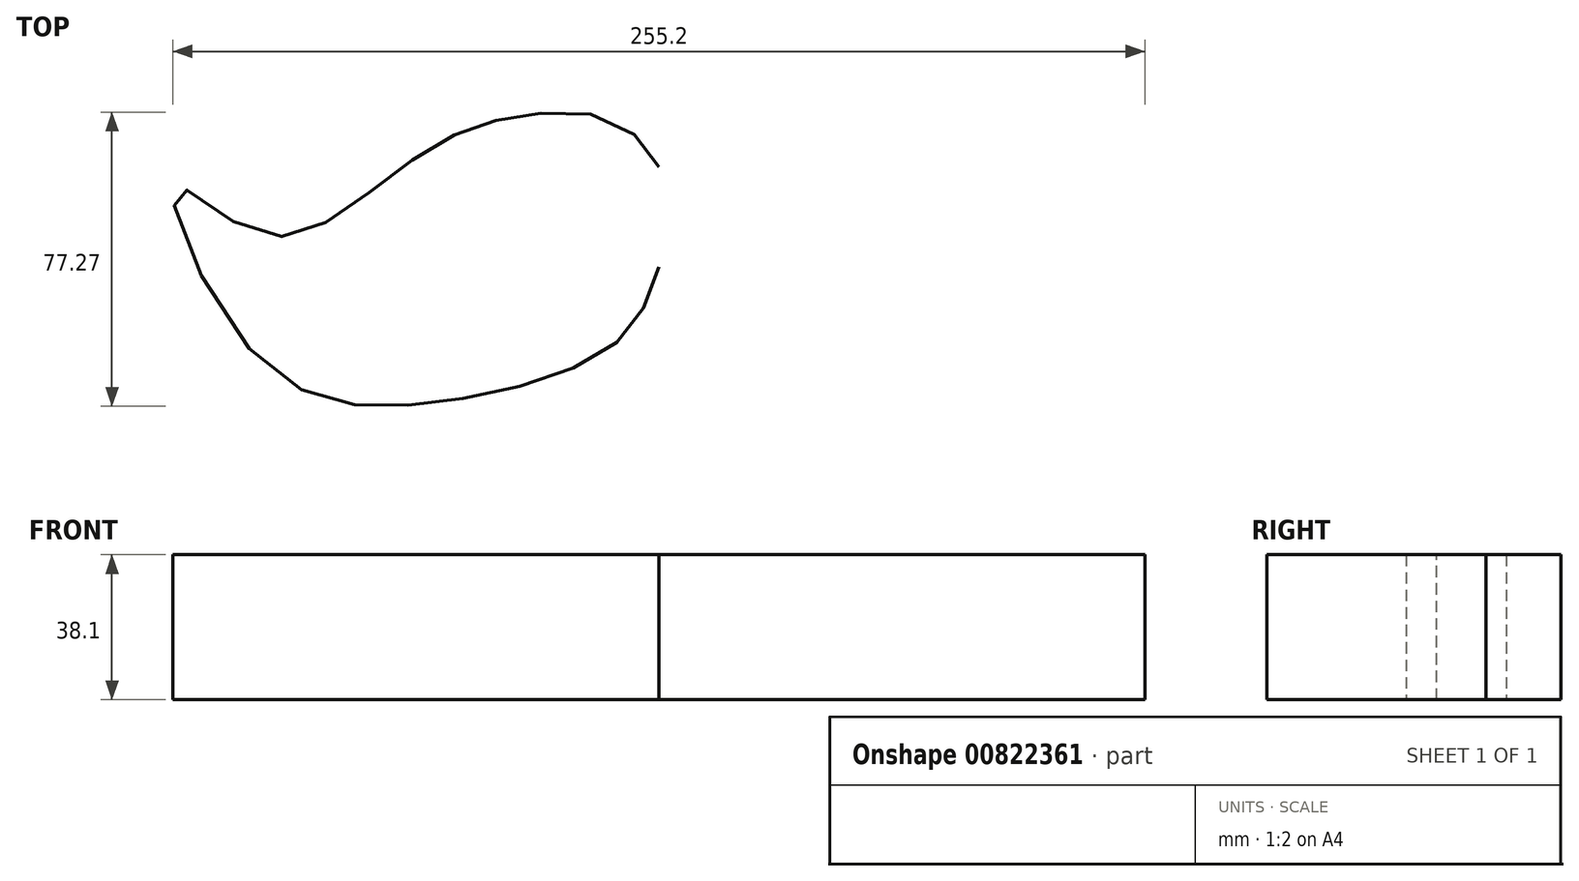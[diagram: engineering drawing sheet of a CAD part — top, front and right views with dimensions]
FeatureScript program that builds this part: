
annotation { "Feature Type Name" : "Feature", "Feature Type Description" : "" }
export const myFeature = defineFeature(function(context is Context, id is Id, definition is map)
    precondition{}
    {
        {
            var Q0;
            Q0=qCreatedBy(makeId("Top.planeOp"),FACE);
            var sketch = newSketch(context, id + "F0", { "sketchPlane" : qUnion([Q0])});
            skLineSegment(sketch, "E0", {"start": v(0, 0) * mm, "end": v(0, 53.62) * mm, "construction": true});
            skLineSegment(sketch, "E1", {"start": v(0, -11.46) * mm, "end": v(0, -32.17) * mm});
            skPoint(sketch, "E2.7.internal.snap0", {"position": v(0, -21.81) * mm});
            skPoint(sketch, "E2.8.internal.snap0", {"position": v(0, -21.81) * mm});
            skFitSpline(sketch, "E2", {"points": [v(0, -32.17) * mm, v(-6.94, -47.84) * mm, v(-25.13, -59.87) * mm, v(-54.24, -67.15) * mm, v(-80.54, -68.27) * mm, v(-109.65, -51.2) * mm, v(-127, -11.46) * mm, v(-109.09, -21.81) * mm, v(-90.06, -21.81) * mm, v(-69.07, -7.26) * mm, v(-50.32, 3.93) * mm, v(-32.97, 7.93) * mm, v(-11.42, 5.9) * mm, v(0, -5.86) * mm, v(0, -11.46) * mm], "startDerivative": vector(-93.95, -278.08) * mm, "endDerivative": vector(-33.34, -168.23) * mm});
            skFitSpline(sketch, "E3.MirrorCS", {"points": [v(0, -32.17) * mm, v(6.94, -47.84) * mm, v(25.13, -59.87) * mm, v(54.24, -67.15) * mm, v(80.54, -68.27) * mm, v(109.65, -51.2) * mm, v(127, -11.46) * mm, v(109.09, -21.81) * mm, v(90.06, -21.81) * mm, v(69.07, -7.26) * mm, v(50.32, 3.93) * mm, v(32.97, 7.93) * mm, v(11.42, 5.9) * mm, v(0, -5.86) * mm, v(0, -11.46) * mm], "startDerivative": vector(93.95, -278.08) * mm, "endDerivative": vector(33.34, -168.23) * mm});
            skSolve(sketch);
        }
        {
            var Q0;
            Q0 = qSketchRegion(id + "F0", true);
            extrude(context, id + "F1", {"entities" : qUnion([Q0]), "depth" : 38.1 * mm, "offsetDistance" : 25.4 * mm});
        }
    });
